# Revit family: 0048730
name_source: partatom
category: Lighting Fixtures
revit_build: Autodesk Revit 2017 (Build: 20190507_1515(x64)
units: mm (PartAtom-declared; Revit-internal decimal feet)

## family parameters
Cut with Voids When Loaded = No
Host = Face
Light Source = Yes
OmniClass Number = 23.80.70.11.14
OmniClass Title = General Luminaries, Directional
Part Type = Normal
Room Calculation Point = No
Round Connector Dimension = Use Diameter
Shared = No

## types (2) — shared parameters
AccessoryMaterial = Diffuser-Sylvania-Glow
Assembly Code = D5020200
AssetType = Fixed
BodyMaterial = Body-Sylvania-Gray
ClassificationName = Uniclass2015
ClassificationValue = EF_70_80
Color Filter = 16777215
Default Elevation = 1219 mm
Description = Sylproof Superia, integrated LED weatherproof luminaire, with UV stabilized flat diffuser and linear prisms designed to achieve uniform lit appearance, optimise light output and to reduce glare, stainless steel diffuser clips and fixing brackets for surface and wall mounting. L 1578 mm x W 110 mm x H 78 mm size, Polycarbonate housing, Polycarbonate diffuser, Non dimmable,   3 hour emergency, 4000K, CRI80,  6700 lm, 49 W, 135 lm/W, nominal average life (h):50000, energy class: A++ A+ A Class I,IK08, IP65.
DiffuserMaterial = Diffuser-Sylvania-Transparent
Dimming Lamp Color Temperature Shift = <None>
DimmingControlOptions = Non dimmable
DocumentationLiterature = http://www.sylvania-lighting.com
DurationUnit = hours
ElectricShockClassification = Class I
Emit Shape Visible in Rendering = No
Emit from Rectangle Length = 1552 mm  [stored 5.09186 ft]
Emit from Rectangle Width = 90 mm  [stored 0.295276 ft]
ExpectedLife = 50000
IfcExportAs = IfcLightFixtureType
IfcExportType = IfcLightFixtureType
ImpactProtectionIndex = IK08
IngressProtection = IP65
InputNominalFrequency = 50/60 Hz
InputVoltage = 220-240V~
Keynote = 16500
Lamp = LED
LampColourRenderingIndex = 80
LampColourTemperature = 4000 K
LampMacAdamStep = 3
LampsType = LED
Length = 1572 mm  [stored 5.15748 ft]
Manufacturer = Feilo Sylvania
ManufacturerName = Feilo Sylvania
Material = polycarbonate housing, polycarbonate diffuser
Model = SYLPRF SUP LED G3 1500MM T 4K E3 SSH01
ModelNumber = 0048730
ModelReference = SYLPRF SUP LED G3 1500MM T 4K E3 SSH01
Name = SYLPRF SUP LED G3 1500MM T 4K E3 SSH01
NominalHeight = 78 mm  [stored 0.255906 ft]
NominalLength = 1578 mm  [stored 5.17717 ft]
ReflectorMaterial = <By Category>
Tilt Angle = -90.00°
Type Image = <None>
TypeName = SYLPRF SUP LED G3 1500MM T 4K E3 SSH01
URL = http://www.sylvania-lighting.com
Voltage = 230 V
Weight = 2.6 kg
Width = 110 mm  [stored 0.360892 ft]
zero-valued in all types: Cost, NominalWidth, PowerFactor

## per-type parameters (varying)
| type | Apparent Load | LampNominalLuminous | LuminousEfficacy | Photometric Web File | PowerConsumption |
| 0048730 SYLPRF SUP LED G3 1500MM T 4K E3 SSH01 Emergency mode | 1 VA | 200 lm | 135 lm/W | 0048730EM.ies | 1.48 W |
| 0048730 SYLPRF SUP LED G3 1500MM T 4K E3 SSH01 | 51 VA | 6800 lm | 133.33 lm/W | 0048730.ies | 51 W |

note: [stored X ft] marks values corroborated as IEEE doubles in the binary element streams (Revit-internal decimal feet)

## geometry (parser evidence)
native form markers: Sweep x3
no freeform markers — native parametric forms only
